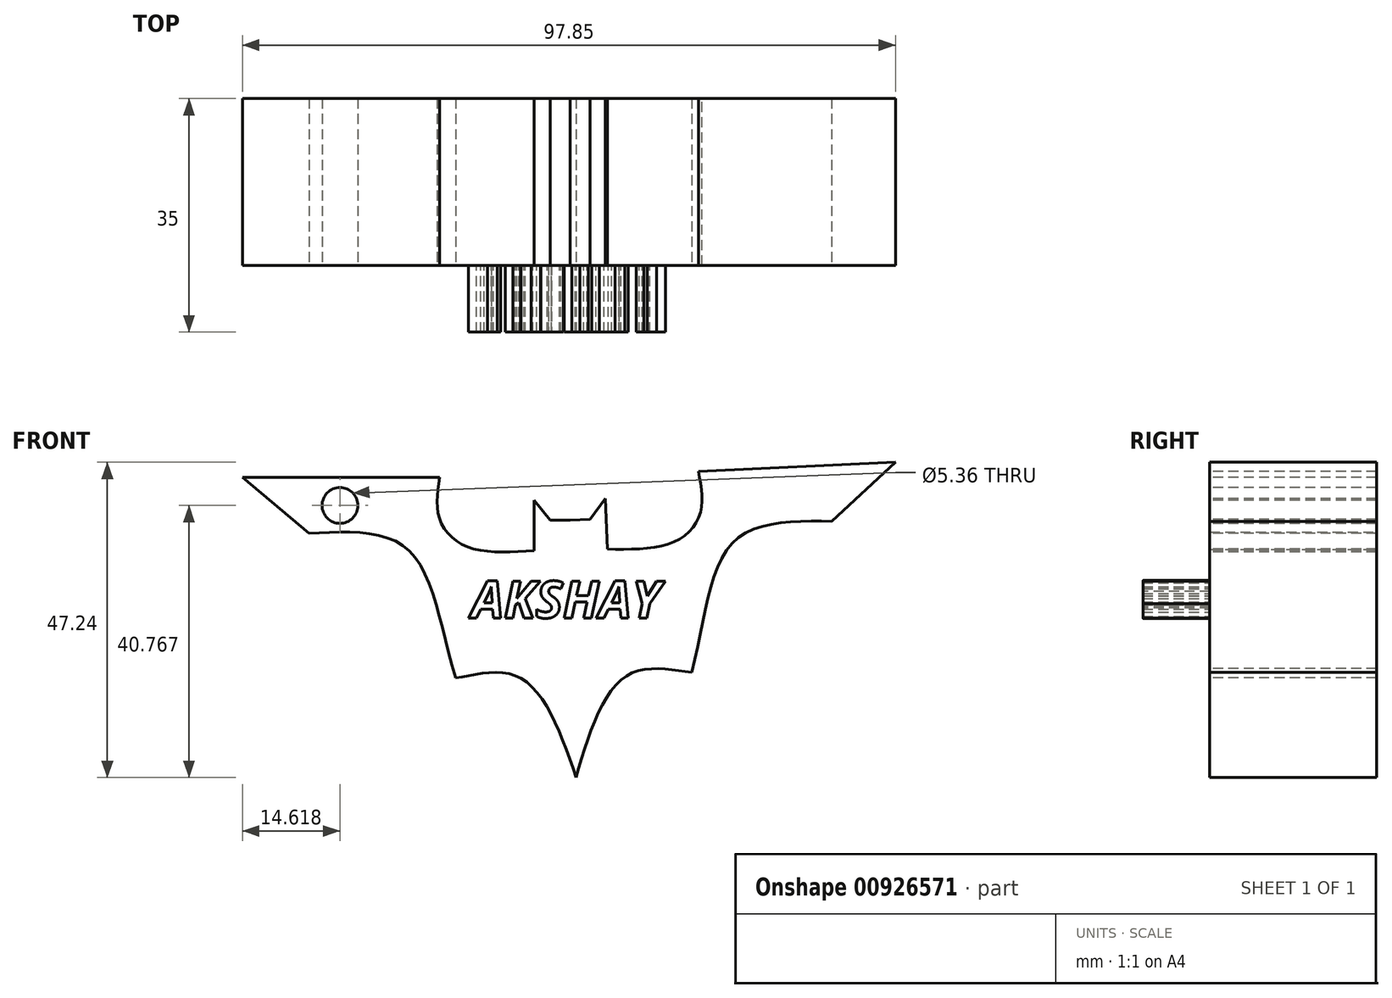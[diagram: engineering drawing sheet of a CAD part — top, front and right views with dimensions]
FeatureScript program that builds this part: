
annotation { "Feature Type Name" : "Feature", "Feature Type Description" : "" }
export const myFeature = defineFeature(function(context is Context, id is Id, definition is map)
    precondition{}
    {
        {
            var Q0;
            Q0=qCreatedBy(makeId("Front.planeOp"),FACE);
            var sketch = newSketch(context, id + "F0", { "sketchPlane" : qUnion([Q0])});
            skLineSegment(sketch, "E0", {"start": v(-50, 15.47) * mm, "end": v(-20.46, 15.47) * mm});
            skFitSpline(sketch, "E1", {"points": [v(-20.46, 15.47) * mm, v(-20.46, 9.28) * mm, v(-16.27, 5.09) * mm, v(-6.29, 4.5) * mm], "startDerivative": vector(-2.73, -20.8) * mm, "endDerivative": vector(28.17, 1.86) * mm});
            skLineSegment(sketch, "E2", {"start": v(-6.29, 4.5) * mm, "end": v(-6.29, 12.08) * mm});
            skLineSegment(sketch, "E3", {"start": v(-6.29, 12.08) * mm, "end": v(-3.9, 9.08) * mm});
            skLineSegment(sketch, "E4", {"start": v(-3.9, 9.08) * mm, "end": v(0, 9.08) * mm});
            skLineSegment(sketch, "E5", {"start": v(-50, 15.47) * mm, "end": v(-40.02, 7.09) * mm});
            skFitSpline(sketch, "E6", {"points": [v(-40.02, 7.09) * mm, v(-25.45, 4.9) * mm, v(-18.02, -14.57) * mm], "startDerivative": vector(34.84, 1.94) * mm, "endDerivative": vector(13.41, -43.86) * mm});
            skFitSpline(sketch, "E7", {"points": [v(-18.02, -14.57) * mm, v(-8.34, -14.57) * mm, v(0, -29.49) * mm], "startDerivative": vector(21.71, 3.87) * mm, "endDerivative": vector(10.72, -32.28) * mm});
            skLineSegment(sketch, "E8", {"start": v(-0.9, 9.08) * mm, "end": v(0, -29.49) * mm});
            skPoint(sketch, "E9.start.orphan", {"position": v(4.3, 12.08) * mm});
            skPoint(sketch, "E10.orphan", {"position": v(2.1, 9.08) * mm});
            skPoint(sketch, "E11.0.internal.orphan", {"position": v(17.07, 15.47) * mm});
            skPoint(sketch, "E11.1.internal.orphan", {"position": v(17.66, 9.28) * mm});
            skPoint(sketch, "E11.2.internal.orphan", {"position": v(15.67, 4.9) * mm});
            skPoint(sketch, "E11.3.internal.orphan", {"position": v(4.3, 4.5) * mm});
            skPoint(sketch, "E12.1.internal.orphan", {"position": v(26.65, 7.09) * mm});
            skPoint(sketch, "E12.2.internal.orphan", {"position": v(15.67, -14.87) * mm});
            skPoint(sketch, "E13.end.orphan", {"position": v(50, 15.47) * mm});
            skPoint(sketch, "E13.start.orphan", {"position": v(38.82, 7.09) * mm});
            skPoint(sketch, "E14.1.internal.orphan", {"position": v(6.09, -14.57) * mm});
            skLineSegment(sketch, "E15.MirrorCS", {"start": v(4.7, 4.75) * mm, "end": v(4.35, 12.32) * mm});
            skLineSegment(sketch, "E16.MirrorCS", {"start": v(4.35, 12.32) * mm, "end": v(2.1, 9.22) * mm});
            skLineSegment(sketch, "E17.MirrorCS", {"start": v(2.1, 9.22) * mm, "end": v(-1.8, 9.04) * mm});
            skFitSpline(sketch, "E18.MirrorCS", {"points": [v(18.34, 16.37) * mm, v(18.63, 10.2) * mm, v(14.64, 5.8) * mm, v(4.7, 4.75) * mm], "startDerivative": vector(3.7, -20.66) * mm, "endDerivative": vector(-28.22, 0.54) * mm});
            skLineSegment(sketch, "E19.MirrorCS", {"start": v(47.85, 17.75) * mm, "end": v(18.34, 16.37) * mm});
            skLineSegment(sketch, "E20.MirrorCS", {"start": v(47.85, 17.75) * mm, "end": v(38.27, 8.9) * mm});
            skFitSpline(sketch, "E21.MirrorCS", {"points": [v(38.27, 8.9) * mm, v(23.82, 6.04) * mm, v(17.31, -13.74) * mm], "startDerivative": vector(-34.89, 0.31) * mm, "endDerivative": vector(-11.36, -44.44) * mm});
            skFitSpline(sketch, "E22.MirrorCS", {"points": [v(17.31, -13.74) * mm, v(7.64, -14.2) * mm, v(0, -29.49) * mm], "startDerivative": vector(-21.87, 2.85) * mm, "endDerivative": vector(-9.2, -32.74) * mm});
            skSolve(sketch);
        }
        {
            var Q0;
            Q0 = qSketchRegion(id + "F0", true);
            extrude(context, id + "F1", {"entities" : qUnion([Q0]), "oppositeDirection" : true, "depth" : 25 * mm, "offsetDistance" : 25 * mm});
        }
        {
            var Q0;
            Q0=makeQuery(id+"F1.opExtrude","CAP_FACE",FACE,{"disambiguationData":[OSD([sQuery(id+"F0.wireOp",EDGE,"E0"),sQuery(id+"F0.wireOp",EDGE,"E1"),sQuery(id+"F0.wireOp",EDGE,"E2"),sQuery(id+"F0.wireOp",EDGE,"E3"),sQuery(id+"F0.wireOp",EDGE,"E4"),sQuery(id+"F0.wireOp",EDGE,"E9"),sQuery(id+"F0.wireOp",EDGE,"1x4LMoUY-GHw5-GCRU-KKam-mdfSURZnLc7z"),sQuery(id+"F0.wireOp",EDGE,"E11"),sQuery(id+"F0.wireOp",EDGE,"UpFBnPFM-tNdc-IMxa-jMBq-Xcz7DzBH6spp"),sQuery(id+"F0.wireOp",EDGE,"E5"),sQuery(id+"F0.wireOp",EDGE,"E6"),sQuery(id+"F0.wireOp",EDGE,"E13"),sQuery(id+"F0.wireOp",EDGE,"E12"),sQuery(id+"F0.wireOp",EDGE,"E7"),sQuery(id+"F0.wireOp",EDGE,"E14")])],"isStart":true});
            var sketch = newSketch(context, id + "F2", { "sketchPlane" : qUnion([Q0])});
            skText(sketch, "E23", { "text": "AKSHAY", "fontName": "OpenSans-BoldItalic.ttf"});
            const initialGuessF2  = {"E23": [-0.01568, -0.00557, 1, 0, 0.00557]};
            skSetInitialGuess(sketch, initialGuessF2);
            skSolve(sketch);
        }
        {
            var Q0;
            Q0 = qSketchRegion(id + "F2", true);
            extrude(context, id + "F3", {"entities" : qUnion([Q0]), "operationType" : NewBodyOperationType.ADD, "depth" : 10 * mm, "offsetDistance" : 25 * mm});
        }
        {
            var Q0;
            {var subQ0=sQuery(id+"F0.wireOp",EDGE,"UpFBnPFM-tNdc-IMxa-jMBq-Xcz7DzBH6spp");var subQ1=sQuery(id+"F0.wireOp",EDGE,"E11");var subQ2=sQuery(id+"F0.wireOp",EDGE,"1x4LMoUY-GHw5-GCRU-KKam-mdfSURZnLc7z");var subQ3=sQuery(id+"F0.wireOp",EDGE,"E9");var subQ4=sQuery(id+"F0.wireOp",EDGE,"E4");var subQ5=sQuery(id+"F0.wireOp",EDGE,"E5");var subQ6=sQuery(id+"F0.wireOp",EDGE,"E0");var subQ7=sQuery(id+"F0.wireOp",EDGE,"E3");var subQ8=sQuery(id+"F0.wireOp",EDGE,"E1");var subQ9=sQuery(id+"F0.wireOp",EDGE,"E2");var subQ10=sQuery(id+"F0.wireOp",EDGE,"E6");var subQ11=sQuery(id+"F0.wireOp",EDGE,"E13");var subQ12=sQuery(id+"F0.wireOp",EDGE,"E12");var subQ13=sQuery(id+"F0.wireOp",EDGE,"E7");var subQ14=sQuery(id+"F0.wireOp",EDGE,"E14");Q0=makeQuery(id+"F3.boolean.opBoolean","SPLIT",FACE,{"disambiguationData":[TD([makeQuery(id+"F1.opExtrude","SWEPT_FACE",FACE,{"disambiguationData":[OSD([subQ6])]})])],"derivedFrom":makeQuery(id+"F1.opExtrude","CAP_FACE",FACE,{"disambiguationData":[OSD([subQ6,subQ8,subQ9,subQ7,subQ4,subQ3,subQ2,subQ1,subQ0,subQ5,subQ10,subQ11,subQ12,subQ13,subQ14])],"isStart":true})});}
            var sketch = newSketch(context, id + "F4", { "sketchPlane" : qUnion([Q0])});
            skCircle(sketch, "E24", {"center": v(-35.38, 11.28) * mm, "radius": 2.68 * mm});
            skPoint(sketch, "E24.centerSnap0", {"position": v(44.41, 11.28) * mm});
            skSolve(sketch);
        }
        {
            var Q0;
            Q0=makeQuery(id+"F4.imprint","IMPRINT",FACE,{"disambiguationData":[TD([[makeQuery(id+"F4.imprint","IMPRINT",EDGE,{"derivedFrom":sQuery(id+"F4.wireOp",EDGE,"E24")}),1.0]])]});
            extrude(context, id + "F5", {"entities" : qUnion([Q0]), "operationType" : NewBodyOperationType.REMOVE, "endBound" : BoundingType.THROUGH_ALL, "oppositeDirection" : true, "depth" : 25 * mm, "offsetDistance" : 25 * mm});
        }
    });
